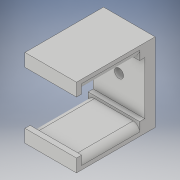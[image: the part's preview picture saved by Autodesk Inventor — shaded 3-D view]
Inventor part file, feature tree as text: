
AUTODESK INVENTOR PART (.ipt)
format: ipt  version: 2019 (Build 230136000, 136)  size: 158,720 bytes
history: native  units: in
note: dims shown in document units (in); Inventor stores cm internally (conversion verified against a paired STEP export)
features: sketch x5, extrude x4, fillet x1, hole x1
ambient origin geometry x8: Origin, YZ Plane, XZ Plane, XY Plane, X Axis, Y Axis, Z Axis, Center Point
bodies: Solid1 (feature_tree)
feature tree (11):
  extrude  "Extrusion1"  Depth=1.525in
  extrude  "Extrusion4"  Depth=0.2in
  extrude  "Extrusion5"  TaperAngle=0.0deg  [1 undecoded]
  extrude  "Extrusion6"  Depth=0.2in
  fillet  "Fillet2"  Radius=0.25in
  hole  "Hole2"  [1 undecoded]
  sketch  "Sketch1"  dims[d0=1.0in d1=1.525in]
  sketch  "Sketch5"  dims[d2=0.3in d3=0.0in d29=0.2in]
  sketch  "Sketch6"  dims[d30=0.2in d31=0.0in]
  sketch  "Sketch7"  dims[d32=1.125in d33=0.0in d34=0.2in d35=0.25in]
  sketch  "Sketch8"  dims[d36=0.25in d37=1.0in d38=1.0in d39=0.1in d40=0.0in d41=1.025in d42=0.05in d43=1.0in d44=0.1in d45=0.0in d46=0.125in d47=0.5in d48=1.0in d49=1.525in d50=0.7625in d51=0.177in d52=0.75in d53=0.332in d54=0.25in d55=0.5635in d56=1.0in d57=0.8108in]
note: 2 required parameter values undecoded (feature->parameter linkage not recoverable at this tier; creation-order binding heuristic only, values carry confidence <= 0.55)
